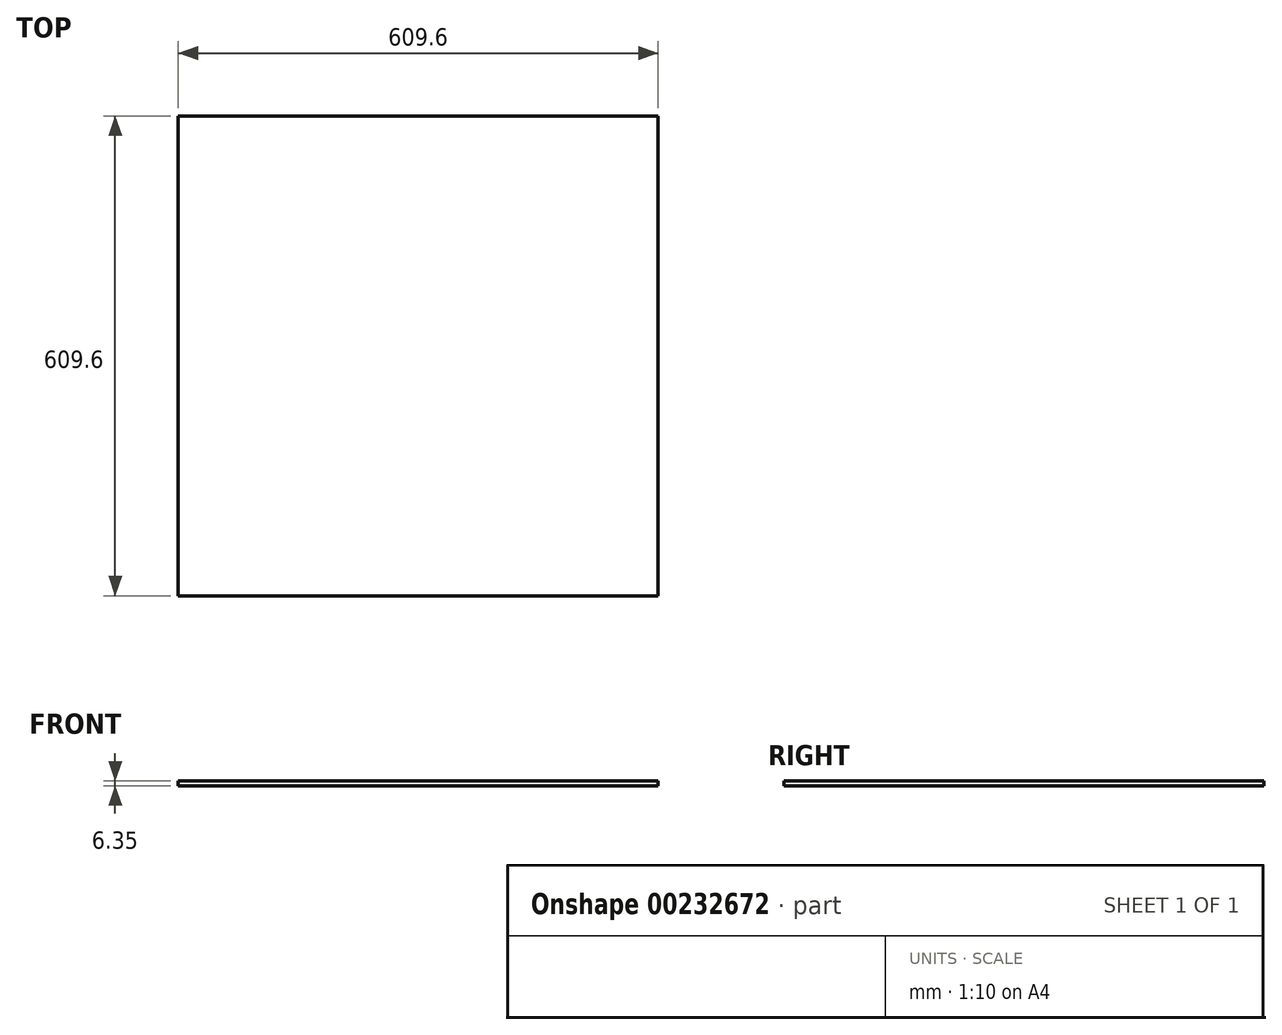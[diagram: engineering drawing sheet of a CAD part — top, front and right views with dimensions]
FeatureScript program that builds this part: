
annotation { "Feature Type Name" : "Feature", "Feature Type Description" : "" }
export const myFeature = defineFeature(function(context is Context, id is Id, definition is map)
    precondition{}
    {
        {
            var Q0;
            Q0=qCreatedBy(makeId("Top.planeOp"),FACE);
            var sketch = newSketch(context, id + "F0", { "sketchPlane" : qUnion([Q0])});
            skLineSegment(sketch, "E0.bottom", {"start": v(-304.8, 304.8) * mm, "end": v(304.8, 304.8) * mm});
            skLineSegment(sketch, "E0.top", {"start": v(-304.8, -304.8) * mm, "end": v(304.8, -304.8) * mm});
            skLineSegment(sketch, "E0.left", {"start": v(-304.8, 304.8) * mm, "end": v(-304.8, -304.8) * mm});
            skLineSegment(sketch, "E0.right", {"start": v(304.8, 304.8) * mm, "end": v(304.8, -304.8) * mm});
            skPoint(sketch, "E0.middle", {"position": v(0, 0) * mm});
            skSolve(sketch);
        }
        {
            var Q0;
            Q0 = qSketchRegion(id + "F0", true);
            extrude(context, id + "F1", {"entities" : qUnion([Q0]), "depth" : 6.35 * mm});
        }
    });
